# Revit family: NICE200COB
name_source: partatom
category: Lighting Fixtures
units: mm (PartAtom-declared; Revit-internal decimal feet)

## family parameters
Cut with Voids When Loaded = No
Host = Face
Light Source = Yes
Maintain Annotation Orientation = Yes
Part Type = Normal
Room Calculation Point = No
Round Connector Dimension = Use Diameter
Shared = No

## types (20) — shared parameters
Color Filter = 16777215
Default Elevation = 1219 mm
Dimming Lamp Color Temperature Shift = <None>
Emit from Line Length = 610 mm
Manufacturer = LUXLIGHT
Tilt Angle = 0.00°
zero-valued in all types: LuxLight_Alto, LuxLight_AltoAreaLuminosa, LuxLight_Ancho, LuxLight_AnchoAreaLuminosa, LuxLight_Diametro, LuxLight_DiametroAreaLuminosa, LuxLight_Largo, LuxLight_LargoAreaLuminosa, LuxLight_ProtuberanciaTecho

## per-type parameters (varying)
| type | LuxLight_Amperios | LuxLight_Lumenes | LuxLight_Temperatura | LuxLight_Watios | Photometric Web File |
| LXRNI200COB192x | 350 | 1466 lm | 2700 K | 15 W | LXRNI200COB1921_15W_2700K .ies |
| LXRNI200COB193x | 350 | 1566 lm | 3000 K | 15 W | LXRNI200COB1931_15W_3000K .ies |
| LXRNI200COB1935x | 350 | 1632 lm | 3500 K | 15 W | LXRNI200COB19351_15W_3500K .ies |
| LXRNI200COB194x | 350 | 1742 lm | 4000 K | 15 W | LXRNI200COB1941_15W_4000K .ies |
| LXRNI200COB292x | 500 | 1988 lm | 2700 K | 20 W | LXRNI200COB2921_20W_2700K .ies |
| LXRNI200COB293x | 500 | 2088 lm | 3000 K | 20 W | LXRNI200COB2931_20W_3000K .ies |
| LXRNI200COB2935x | 500 | 2176 lm | 3500 K | 20 W | LXRNI200COB29351_20W_3500K .ies |
| LXRNI200COB294x | 500 | 2286 lm | 4000 K | 20 W | LXRNI200COB2941_20W_4000K .ies |
| LXRNI200COB392x | 700 | 2510 lm | 2700 K | 25 W | LXRNI200COB3921_25W_2700K .ies |
| LXRNI200COB393x | 700 | 2610 lm | 3000 K | 25 W | LXRNI200COB3931_25W_3000K .ies |
| LXRNI200COB3935x | 700 | 2720 lm | 3500 K | 25 W | LXRNI200COB39351_25W_3500K .ies |
| LXRNI200COB394x | 700 | 2830 lm | 4000 K | 25 W | LXRNI200COB3941_25W_4000K .ies |
| LXRNI200COB492x | 800 | 3032 lm | 2700 K | 30 W | LXRNI200COB4921_30W_2700K .ies |
| LXRNI200COB493x | 800 | 3132 lm | 3000 K | 30 W | LXRNI200COB4931_30W_3000K .ies |
| LXRNI200COB4935x | 800 | 3264 lm | 3500 K | 30 W | LXRNI200COB49351_30W_3500K .ies |
| LXRNI200COB494x | 800 | 3374 lm | 4000 K | 30 W | LXRNI200COB4941_30W_4000K .ies |
| LXRNI200COB592x | 1050 | 4076 lm | 2700 K | 40 W | LXRNI200COB5921_40W_2700K .ies |
| LXRNI200COB593x | 1050 | 4176 lm | 3000 K | 40 W | LXRNI200COB5931_40W_3000K .ies |
| LXRNI200COB5935x | 1050 | 4352 lm | 3500 K | 40 W | LXRNI200COB59351_40W_3500K .ies |
| LXRNI200COB594x | 1050 | 4462 lm | 4000 K | 40 W | LXRNI200COB5941_40W_4000K .ies |

## geometry (parser evidence)
native form markers: Sweep x3
no freeform markers — native parametric forms only
